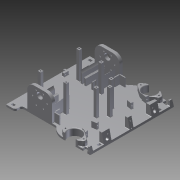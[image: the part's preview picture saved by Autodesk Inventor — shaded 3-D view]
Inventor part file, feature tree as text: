
AUTODESK INVENTOR PART (.ipt)
format: ipt  version: 2011 SP2 (Build 150309200, 309)  size: 1,229,824 bytes
history: native  units: mm
features: extrude x35, sketch x21, projected_geometry x14, fillet x12, mirror x2, plane x1, chamfer x1, hole x1
ambient origin geometry x8: Origin, YZ Plane, XZ Plane, XY Plane, X Axis, Y Axis, Z Axis, Center Point
feature tree (87):
  sketch  "Sketch1"  dims[d0=200.0mm d1=200.0mm]
  extrude  "Extrusion3"  Depth=200.0mm
  extrude  "Extrusion4"  Depth=10.5mm
  extrude  "Extrusion5"  Depth=6.5mm
  extrude  "Extrusion6"  Depth=53.3mm
  extrude  "Extrusion7"  Depth=26.65mm
  sketch  "Sketch4"  dims[d6=6.5mm d8=53.3mm]
  extrude  "Extrusion8"  Depth=5.0mm
  extrude  "Extrusion9"  Depth=5.0mm
  extrude  "Extrusion10"  Depth=4.6mm
  plane  "Work Plane1"
  mirror  "Mirror1"
  sketch  "Sketch9"  dims[d9=53.3mm d10=26.65mm]
  sketch  "Sketch10"  dims[d11=26.65mm d13=5.0mm]
  extrude  "Extrusion16"  Depth=8.0mm
  extrude  "Extrusion17"  Depth=8.0mm
  extrude  "Extrusion18"  Depth=138.0mm
  extrude  "Extrusion19"  Depth=3.0mm
  extrude  "Extrusion20"  Depth=12.061mm
  extrude  "Extrusion21"  Depth=4.0mm TaperAngle=0.0deg
  extrude  "Extrusion22"  Depth=55.0mm TaperAngle=0.0deg
  sketch  "Sketch13"  dims[d18=4.6mm d19=8.0mm]
  extrude  "Extrusion26"  Depth=38.0mm
  extrude  "Extrusion27"  Depth=7.0mm
  extrude  "Extrusion30"  Depth=15.5mm
  extrude  "Extrusion32"  Depth=55.0mm TaperAngle=0.0deg
  extrude  "Extrusion33"  Depth=2.0mm
  extrude  "Extrusion34"  Depth=3.9mm
  chamfer  "Chamfer2"  Distance=55.0mm
  fillet  "Fillet1"  Radius=36.8mm
  extrude  "Extrusion35"  Depth=36.0mm
  extrude  "Extrusion36"  Depth=40.0mm TaperAngle=0.0deg
  sketch  "Sketch21"  dims[d41=6.6mm d42=1.5mm d49=12.061mm]
  extrude  "Extrusion37"  Depth=40.0mm TaperAngle=0.0deg
  extrude  "Extrusion39"  Depth=23.0mm TaperAngle=0.0deg
  extrude  "Extrusion40"  Depth=2.8mm
  fillet  "Fillet2"  Radius=2.8mm
  sketch  "Sketch28"  dims[d64=13.0mm d65=38.0mm]
  extrude  "Extrusion48"  Depth=2.8mm
  extrude  "Extrusion49"  Depth=2.8mm
  extrude  "Extrusion42"  Depth=32.757mm
  extrude  "Extrusion44"  Depth=32.757mm
  fillet  "Fillet4"  Radius=80.957mm
  mirror  "Mirror3"
  fillet  "Fillet3"  Radius=80.957mm
  extrude  "Extrusion45"  Depth=27.264mm
  sketch  "Sketch30"  dims[d68=3.0mm d69=15.5mm]
  extrude  "Extrusion46"  Depth=20.564mm
  extrude  "Extrusion47"  Depth=34.936mm
  hole  "Hole1"  [1 undecoded]
  fillet  "Fillet5"  Radius=2.0mm
  fillet  "Fillet6"  Radius=11.0mm
  fillet  "Fillet7"  Radius=11.0mm
  fillet  "Fillet8"  Radius=2.0mm
  fillet  "Fillet9"  Radius=11.0mm
  fillet  "Fillet10"  Radius=11.0mm
  fillet  "Fillet11"  Radius=2.0mm
  fillet  "Fillet12"  Radius=2.0mm
  extrude  "Extrusion50"  Depth=6.0mm
  extrude  "Extrusion51"  Depth=6.0mm
  sketch  "Sketch2"  dims[d2=10.5mm d3=10.5mm]
  sketch  "Sketch3"  dims[d4=57.861mm d5=6.5mm]
  projected_geometry  "Projected Loop1"
  projected_geometry  "Projected Loop7"
  sketch  "Sketch11"  dims[d14=5.0mm d15=5.0mm]
  sketch  "Sketch12"  dims[d16=6.35mm d17=4.6mm]
  projected_geometry  "Projected Loop8"
  sketch  "Sketch15"  dims[d20=5.0mm d21=8.0mm]
  projected_geometry  "Projected Loop9"
  sketch  "Sketch18"  dims[d22=5.0mm d25=138.0mm]
  projected_geometry  "Projected Loop11"
  sketch  "Sketch20"  dims[d29=3.65mm d30=3.65mm d31=3.0mm d34=1.5mm d37=3.0mm d38=5.0mm]
  projected_geometry  "Projected Loop12"
  sketch  "Sketch25"  dims[d50=5.0mm d58=4.0mm d59=0.0mm]
  sketch  "Sketch27"  dims[d60=11.0mm d61=0.0mm d62=55.0mm d63=0.0mm]
  projected_geometry  "Projected Loop16"
  sketch  "Sketch29"  dims[d66=36.8mm d67=7.0mm]
  sketch  "Sketch31"  dims[d70=60.0mm d72=360.0deg d74=55.0mm d75=0.0mm]
  projected_geometry  "Projected Loop17"
  projected_geometry  "Projected Loop18"
  projected_geometry  "Projected Loop19"
  projected_geometry  "Projected Loop20"
  projected_geometry  "Projected Loop21"
  projected_geometry  "Projected Loop22"
  projected_geometry  "Projected Loop23"
  sketch  "Sketch32"  dims[d76=2.0mm d77=2.0mm]
  sketch  "Sketch33"  dims[d78=3.9mm d79=3.9mm d80=55.0mm d81=0.0mm d82=36.8mm d83=36.0mm d84=40.0mm d85=0.0mm d86=40.0mm d87=0.0mm d88=23.0mm d89=0.0mm d119=2.8mm d120=2.8mm d121=2.8mm d122=2.8mm d135=32.757mm d136=32.757mm d137=80.957mm d138=80.957mm d139=27.264mm d140=20.564mm d141=34.936mm d142=35.936mm d143=2.0mm d144=11.0mm d145=11.0mm d146=2.0mm d147=11.0mm d148=11.0mm d149=2.0mm d150=2.0mm d155=6.0mm d156=6.0mm d157=6.0mm d158=6.0mm d159=3.0mm d160=3.0mm d161=3.0mm d162=3.0mm d163=6.0mm d164=6.0mm d165=3.0mm d166=3.0mm d167=6.0mm d168=6.0mm d169=3.0mm d170=3.0mm d181=3.0mm d182=3.5mm d184=0.0mm d185=0.0mm d186=200.0mm d187=0.0mm d188=200.0mm d189=0.0mm d190=58.0mm d191=0.0mm d192=18.0mm d193=0.0mm d194=40.0mm d195=0.0mm d196=1.570796mm d197=1.570796mm d198=220.0mm d199=220.0mm d200=10.0mm d201=10.0mm d202=5.0mm d203=7.0mm d204=0.0mm d205=0.0mm d215=32.1mm d231=5.0mm d233=12.0mm d234=0.0mm d239=20.0mm d240=0.0mm d256=6.0mm d257=167.0mm d258=6.2mm d259=6.0mm d260=0.0mm d262=22.75mm d266=10.0mm d267=38.9mm d268=5.5mm d269=32.1mm d272=10.0mm d273=12.2mm d276=12.0mm d277=0.0mm d278=28.5mm d279=10.3mm d280=0.0mm d281=5.0mm d282=0.0mm d283=0.5mm d284=5.3mm d285=45.0deg d286=1.0mm d287=5.0mm d288=0.0mm d289=3.0mm d290=3.0mm d291=10.0mm d292=0.0mm d293=6.35mm d294=4.6mm d295=2.0mm d296=3.0mm d297=10.0mm d298=0.0mm d306=41.0mm d307=0.0mm d308=6.0mm d309=6.0mm d310=2.575mm d311=2.575mm d312=2.0mm d313=2.0mm d315=8.956377mm d316=161.0mm d317=10.0mm d318=7.0mm d319=0.0mm d320=32.5mm d335=32.5mm d336=7.0mm d337=12.0mm d338=9.25mm d339=-0.872665mm d343=1.0mm d344=9.25mm d345=-0.872665mm d346=8.0mm d347=4.0mm d348=10.0mm d349=20.0mm d350=0.0mm d351=179.0mm d352=0.0mm d353=179.0mm d354=0.0mm d355=1.5mm d356=3.5mm d357=3.5mm d358=89.5mm d359=89.5mm d360=5.0mm d361=17.5mm d362=2.0mm d363=6.0mm d364=3.0mm d365=2.0mm d366=90.0deg d367=12.0mm d368=0.0mm d369=6.0mm d370=6.0mm d371=6.0mm d372=6.0mm d373=6.0mm d376=6.0mm d377=2.5mm d378=2.5mm d379=2.5mm d380=3.0mm d382=3.0mm d383=3.0mm d384=3.0mm d386=55.0mm d387=0.0mm d388=40.0mm d389=0.0mm d390=26.0mm d391=69.0mm d392=48.0mm d393=3.0mm d394=13.0mm d395=13.0mm d396=3.0mm d397=1.0mm d398=0.5mm d399=0.5mm d400=1.0mm d401=0.5mm d402=1.0mm d403=15.0mm d404=1.0mm d405=10.0mm d406=0.0mm d407=10.0mm d408=0.0mm d409=30.25mm d410=30.25mm d411=33.0mm d412=33.0mm d413=4.0mm d414=7.0mm d415=7.0mm d416=4.0mm d419=7.15mm d420=7.15mm d421=0.0mm]
note: 1 required parameter value undecoded (feature->parameter linkage not recoverable at this tier; creation-order binding heuristic only, values carry confidence <= 0.55)
